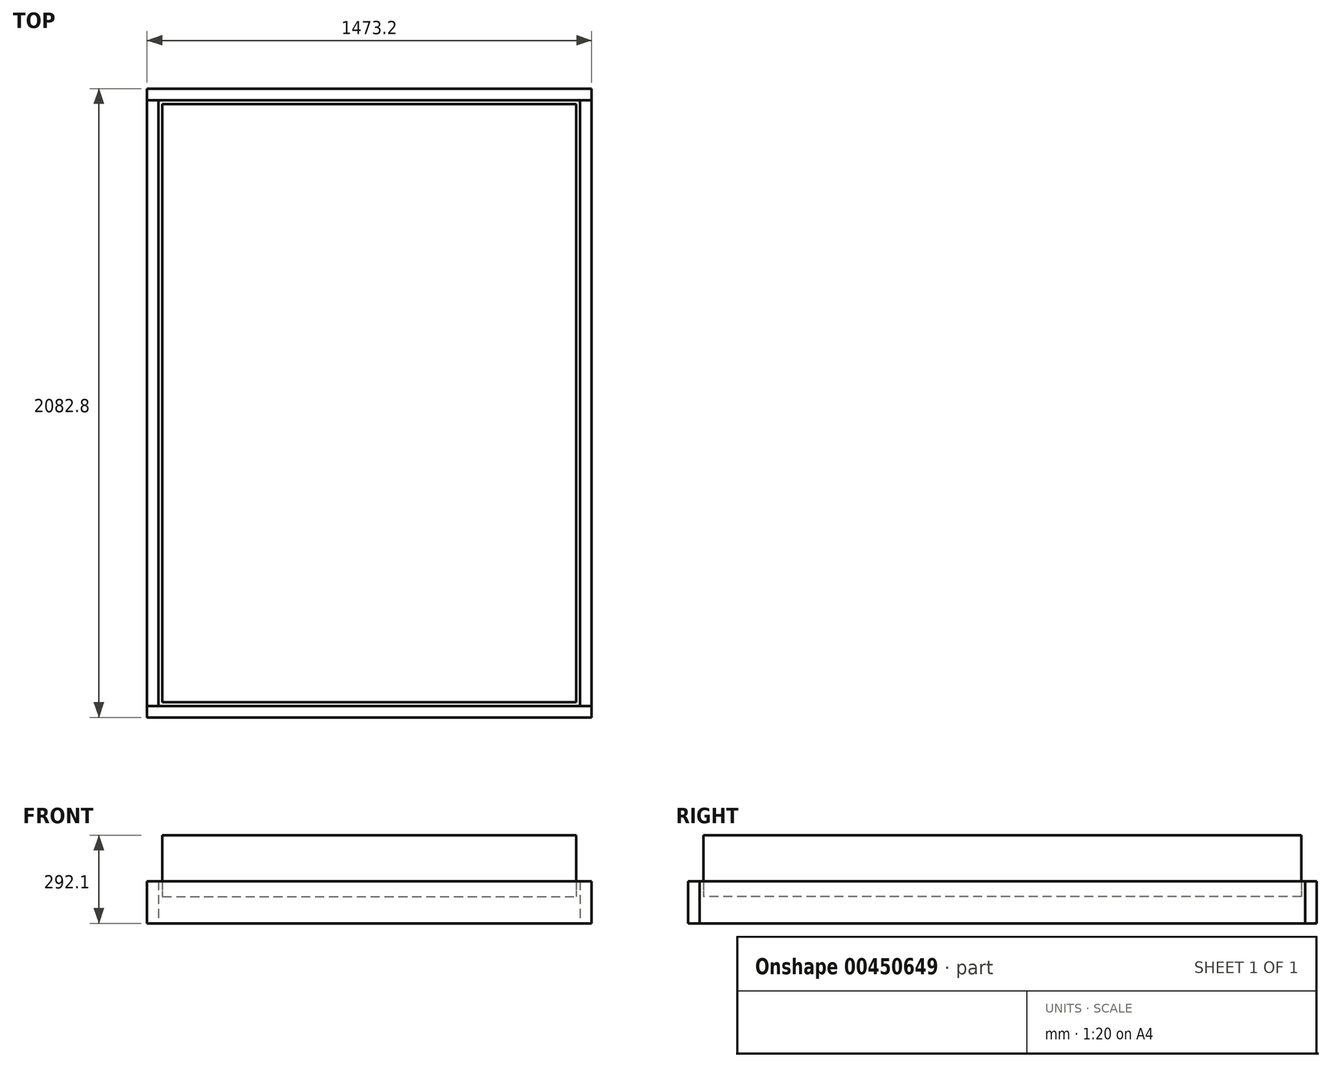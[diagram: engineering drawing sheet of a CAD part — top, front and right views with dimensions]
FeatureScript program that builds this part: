
annotation { "Feature Type Name" : "Feature", "Feature Type Description" : "" }
export const myFeature = defineFeature(function(context is Context, id is Id, definition is map)
    precondition{}
    {
        {
            var Q0;
            Q0=qCreatedBy(makeId("Top.planeOp"),FACE);
            var sketch = newSketch(context, id + "F0", { "sketchPlane" : qUnion([Q0])});
            skLineSegment(sketch, "E0.bottom", {"start": v(-685.8, 990.6) * mm, "end": v(685.8, 990.6) * mm});
            skLineSegment(sketch, "E0.top", {"start": v(-685.8, -990.6) * mm, "end": v(685.8, -990.6) * mm});
            skLineSegment(sketch, "E0.left", {"start": v(-685.8, 990.6) * mm, "end": v(-685.8, -990.6) * mm});
            skLineSegment(sketch, "E0.right", {"start": v(685.8, 990.6) * mm, "end": v(685.8, -990.6) * mm});
            skPoint(sketch, "E0.middle", {"position": v(0, 0) * mm});
            skSolve(sketch);
        }
        {
            var Q0;
            Q0=makeQuery(id+"F0.imprint","IMPRINT",FACE,{"disambiguationData":[TD([[makeQuery(id+"F0.imprint","IMPRINT",EDGE,{"derivedFrom":sQuery(id+"F0.wireOp",EDGE,"E0.bottom")}),-1.0]])]});
            extrude(context, id + "F1", {"entities" : qUnion([Q0]), "depth" : 203.2 * mm});
        }
        {
            var Q0;
            Q0=makeQuery(id+"F1.opExtrude","SWEPT_FACE",FACE,{"disambiguationData":[OSD([sQuery(id+"F0.wireOp",EDGE,"E0.right")])]});
            cPlane(context, id + "F2", {"entities" : qUnion([Q0]), "cplaneType" : CPlaneType.OFFSET, "offset" : 12.7 * mm, "width" : 152.4 * mm, "height" : 152.4 * mm});
        }
        {
            var Q0;
            Q0=qCreatedBy(id+"F2.planeOp",FACE);
            var sketch = newSketch(context, id + "F3", { "sketchPlane" : qUnion([Q0])});
            skLineSegment(sketch, "E1.bottom", {"start": v(-1003.3, 50.8) * mm, "end": v(1003.3, 50.8) * mm});
            skLineSegment(sketch, "E1.top", {"start": v(-1003.3, -88.9) * mm, "end": v(1003.3, -88.9) * mm});
            skLineSegment(sketch, "E1.left", {"start": v(-1003.3, 50.8) * mm, "end": v(-1003.3, -88.9) * mm});
            skLineSegment(sketch, "E1.right", {"start": v(1003.3, 50.8) * mm, "end": v(1003.3, -88.9) * mm});
            skSolve(sketch);
        }
        {
            var Q0;
            Q0=makeQuery(id+"F3.imprint","IMPRINT",FACE,{"disambiguationData":[TD([[makeQuery(id+"F3.imprint","IMPRINT",EDGE,{"derivedFrom":sQuery(id+"F3.wireOp",EDGE,"E1.bottom")}),-1.0]])]});
            extrude(context, id + "F4", {"entities" : qUnion([Q0]), "depth" : 38.1 * mm});
        }
        {
            var Q0;
            Q0=makeQuery(id+"F4.opExtrude","SWEPT_BODY",BODY,{"disambiguationData":[OSD([sQuery(id+"F3.wireOp",EDGE,"E1.bottom"),sQuery(id+"F3.wireOp",EDGE,"E1.top"),sQuery(id+"F3.wireOp",EDGE,"E1.left"),sQuery(id+"F3.wireOp",EDGE,"E1.right")])]});
            var Q1;
            Q1=qCreatedBy(makeId("Right.planeOp"),FACE);
            mirror(context, id + "F5", {"entities" : qUnion([Q0]), "mirrorPlane" : qUnion([Q1])});
        }
        {
            var Q0;
            Q0=makeQuery(id+"F1.opExtrude","SWEPT_FACE",FACE,{"disambiguationData":[OSD([sQuery(id+"F0.wireOp",EDGE,"E0.top")])]});
            cPlane(context, id + "F6", {"entities" : qUnion([Q0]), "cplaneType" : CPlaneType.OFFSET, "offset" : 12.7 * mm, "width" : 152.4 * mm, "height" : 152.4 * mm});
        }
        {
            var Q0;
            Q0=qCreatedBy(id+"F6.planeOp",FACE);
            var sketch = newSketch(context, id + "F7", { "sketchPlane" : qUnion([Q0])});
            skLineSegment(sketch, "E2.bottom", {"start": v(-736.6, 50.8) * mm, "end": v(736.6, 50.8) * mm});
            skLineSegment(sketch, "E2.top", {"start": v(-736.6, -88.9) * mm, "end": v(736.6, -88.9) * mm});
            skLineSegment(sketch, "E2.left", {"start": v(-736.6, 50.8) * mm, "end": v(-736.6, -88.9) * mm});
            skLineSegment(sketch, "E2.right", {"start": v(736.6, 50.8) * mm, "end": v(736.6, -88.9) * mm});
            skSolve(sketch);
        }
        {
            var Q0;
            Q0 = qSketchRegion(id + "F7", true);
            extrude(context, id + "F8", {"entities" : qUnion([Q0]), "depth" : 38.1 * mm});
        }
        {
            var Q0;
            Q0=makeQuery(id+"F8.opExtrude","SWEPT_BODY",BODY,{"disambiguationData":[OSD([sQuery(id+"F7.wireOp",EDGE,"E2.bottom"),sQuery(id+"F7.wireOp",EDGE,"E2.top"),sQuery(id+"F7.wireOp",EDGE,"E2.left"),sQuery(id+"F7.wireOp",EDGE,"E2.right")])]});
            var Q1;
            Q1=qCreatedBy(makeId("Front.planeOp"),FACE);
            mirror(context, id + "F9", {"entities" : qUnion([Q0]), "mirrorPlane" : qUnion([Q1])});
        }
    });
